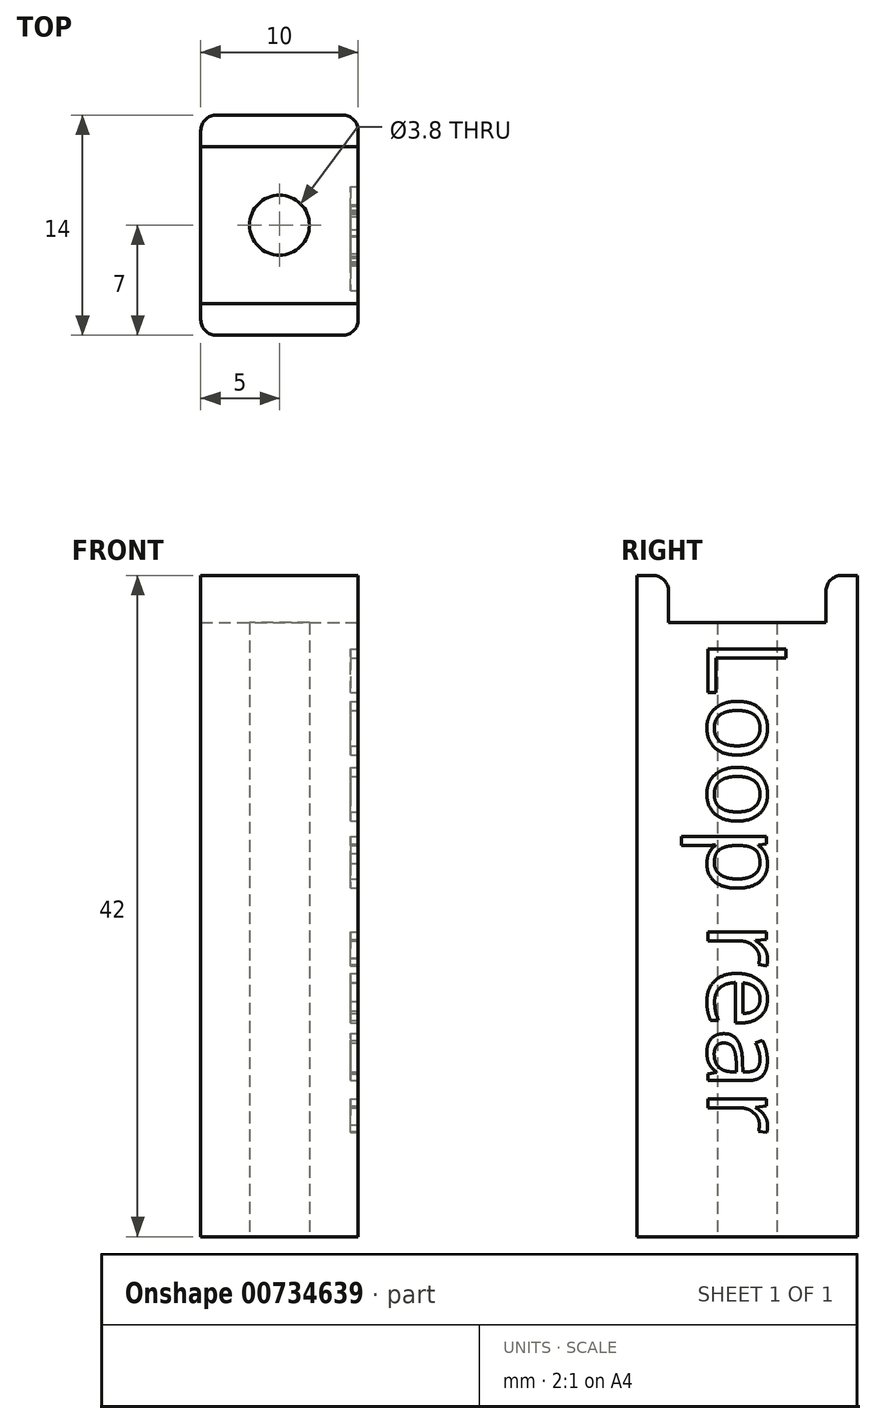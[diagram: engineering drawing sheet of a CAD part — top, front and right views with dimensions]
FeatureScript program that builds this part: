
annotation { "Feature Type Name" : "Feature", "Feature Type Description" : "" }
export const myFeature = defineFeature(function(context is Context, id is Id, definition is map)
    precondition{}
    {
        {
            var Q0;
            Q0=qCreatedBy(makeId("Top.planeOp"),FACE);
            var sketch = newSketch(context, id + "F0", { "sketchPlane" : qUnion([Q0])});
            skLineSegment(sketch, "E0.bottom", {"start": v(5, -7) * mm, "end": v(-5, -7) * mm});
            skLineSegment(sketch, "E0.top", {"start": v(5, 7) * mm, "end": v(-5, 7) * mm});
            skLineSegment(sketch, "E0.left", {"start": v(5, -7) * mm, "end": v(5, 7) * mm});
            skLineSegment(sketch, "E0.right", {"start": v(-5, -7) * mm, "end": v(-5, 7) * mm});
            skPoint(sketch, "E0.middle", {"position": v(0, 0) * mm});
            skCircle(sketch, "E1", {"center": v(0, 0) * mm, "radius": 1.9 * mm});
            skSolve(sketch);
        }
        {
            var Q0;
            Q0 = qSketchRegion(id + "F0", true);
            extrude(context, id + "F1", {"entities" : qUnion([Q0]), "depth" : 39 * mm, "offsetDistance" : 25 * mm});
        }
        {
            var Q0;
            Q0=makeQuery(id+"F1.opExtrude","CAP_FACE",FACE,{"disambiguationData":[OSD([sQuery(id+"F0.wireOp",EDGE,"E0.bottom"),sQuery(id+"F0.wireOp",EDGE,"E0.top"),sQuery(id+"F0.wireOp",EDGE,"E0.left"),sQuery(id+"F0.wireOp",EDGE,"E0.right"),sQuery(id+"F0.wireOp",EDGE,"E1")])],"isStart":false});
            var sketch = newSketch(context, id + "F2", { "sketchPlane" : qUnion([Q0])});
            skLineSegment(sketch, "E2.bottom", {"start": v(-5, 7) * mm, "end": v(5, 7) * mm});
            skLineSegment(sketch, "E2.top", {"start": v(-5, 5) * mm, "end": v(5, 5) * mm});
            skLineSegment(sketch, "E2.left", {"start": v(-5, 7) * mm, "end": v(-5, 5) * mm});
            skLineSegment(sketch, "E2.right", {"start": v(5, 7) * mm, "end": v(5, 5) * mm});
            skLineSegment(sketch, "E3.MirrorCS", {"start": v(-5, -7) * mm, "end": v(-5, -5) * mm});
            skLineSegment(sketch, "E4.MirrorCS", {"start": v(-5, -5) * mm, "end": v(5, -5) * mm});
            skLineSegment(sketch, "E5.MirrorCS", {"start": v(-5, -7) * mm, "end": v(5, -7) * mm});
            skLineSegment(sketch, "E6.MirrorCS", {"start": v(5, -7) * mm, "end": v(5, -5) * mm});
            skSolve(sketch);
        }
        {
            var Q0;
            Q0 = qSketchRegion(id + "F2", true);
            extrude(context, id + "F3", {"entities" : qUnion([Q0]), "operationType" : NewBodyOperationType.ADD, "depth" : 3 * mm, "offsetDistance" : 25 * mm});
        }
        {
            var Q0;
            Q0=makeQuery(id+"F3.boolean.opBoolean","MERGE",EDGE,{"derivedFrom":[makeQuery(id+"F1.opExtrude","SWEPT_EDGE",EDGE,{"disambiguationData":[OSD([sQuery(id+"F0.wireOp",EDGE,"E0.bottom"),sQuery(id+"F0.wireOp",EDGE,"E0.left")])]}),makeQuery(id+"F3.opExtrude","SWEPT_EDGE",EDGE,{"disambiguationData":[OSD([sQuery(id+"F2.wireOp",EDGE,"E5.MirrorCS"),sQuery(id+"F2.wireOp",EDGE,"E6.MirrorCS")])]})]});
            var Q1;
            Q1=makeQuery(id+"F3.boolean.opBoolean","MERGE",EDGE,{"derivedFrom":[makeQuery(id+"F1.opExtrude","SWEPT_EDGE",EDGE,{"disambiguationData":[OSD([sQuery(id+"F0.wireOp",EDGE,"E0.bottom"),sQuery(id+"F0.wireOp",EDGE,"E0.right")])]}),makeQuery(id+"F3.opExtrude","SWEPT_EDGE",EDGE,{"disambiguationData":[OSD([sQuery(id+"F2.wireOp",EDGE,"E3.MirrorCS"),sQuery(id+"F2.wireOp",EDGE,"E5.MirrorCS")])]})]});
            var Q2;
            Q2=makeQuery(id+"F3.boolean.opBoolean","MERGE",EDGE,{"derivedFrom":[makeQuery(id+"F1.opExtrude","SWEPT_EDGE",EDGE,{"disambiguationData":[OSD([sQuery(id+"F0.wireOp",EDGE,"E0.top"),sQuery(id+"F0.wireOp",EDGE,"E0.left")])]}),makeQuery(id+"F3.opExtrude","SWEPT_EDGE",EDGE,{"disambiguationData":[OSD([sQuery(id+"F2.wireOp",EDGE,"E2.bottom"),sQuery(id+"F2.wireOp",EDGE,"E2.right")])]})]});
            var Q3;
            Q3=makeQuery(id+"F3.boolean.opBoolean","MERGE",EDGE,{"derivedFrom":[makeQuery(id+"F1.opExtrude","SWEPT_EDGE",EDGE,{"disambiguationData":[OSD([sQuery(id+"F0.wireOp",EDGE,"E0.top"),sQuery(id+"F0.wireOp",EDGE,"E0.right")])]}),makeQuery(id+"F3.opExtrude","SWEPT_EDGE",EDGE,{"disambiguationData":[OSD([sQuery(id+"F2.wireOp",EDGE,"E2.bottom"),sQuery(id+"F2.wireOp",EDGE,"E2.left")])]})]});
            var Q4;
            Q4=makeQuery(id+"F3.opExtrude","CAP_EDGE",EDGE,{"disambiguationData":[OSD([sQuery(id+"F2.wireOp",EDGE,"E2.top")])],"isStart":false});
            var Q5;
            Q5=makeQuery(id+"F3.opExtrude","CAP_EDGE",EDGE,{"disambiguationData":[OSD([sQuery(id+"F2.wireOp",EDGE,"E4.MirrorCS")])],"isStart":false});
            fillet(context, id + "F4", {"entities" : qUnion([Q0, Q1, Q2, Q3, Q4, Q5]), "tangentPropagation" : true, "radius" : 1 * mm, "defaultsChanged" : false, "vertexSettings" : [], "allowEdgeOverflow" : false});
        }
        {
            var Q0;
            Q0=makeQuery(id+"F3.boolean.opBoolean","MERGE",FACE,{"derivedFrom":[makeQuery(id+"F1.opExtrude","SWEPT_FACE",FACE,{"disambiguationData":[OSD([sQuery(id+"F0.wireOp",EDGE,"E0.left")])]}),makeQuery(id+"F3.opExtrude","SWEPT_FACE",FACE,{"disambiguationData":[OSD([sQuery(id+"F2.wireOp",EDGE,"E2.right")])]}),makeQuery(id+"F3.opExtrude","SWEPT_FACE",FACE,{"disambiguationData":[OSD([sQuery(id+"F2.wireOp",EDGE,"E6.MirrorCS")])]})]});
            var sketch = newSketch(context, id + "F5", { "sketchPlane" : qUnion([Q0])});
            skText(sketch, "E7", { "text": "Loop rear", "fontName": "OpenSans-Regular.ttf"});
            const initialGuessF5  = {"E7": [-0.0025, 0.038, 0, -1, 0.005]};
            skSetInitialGuess(sketch, initialGuessF5);
            skSolve(sketch);
        }
        {
            var Q0;
            Q0 = qSketchRegion(id + "F5", true);
            extrude(context, id + "F6", {"entities" : qUnion([Q0]), "operationType" : NewBodyOperationType.REMOVE, "oppositeDirection" : true, "depth" : 0.5 * mm, "offsetDistance" : 25 * mm});
        }
    });
